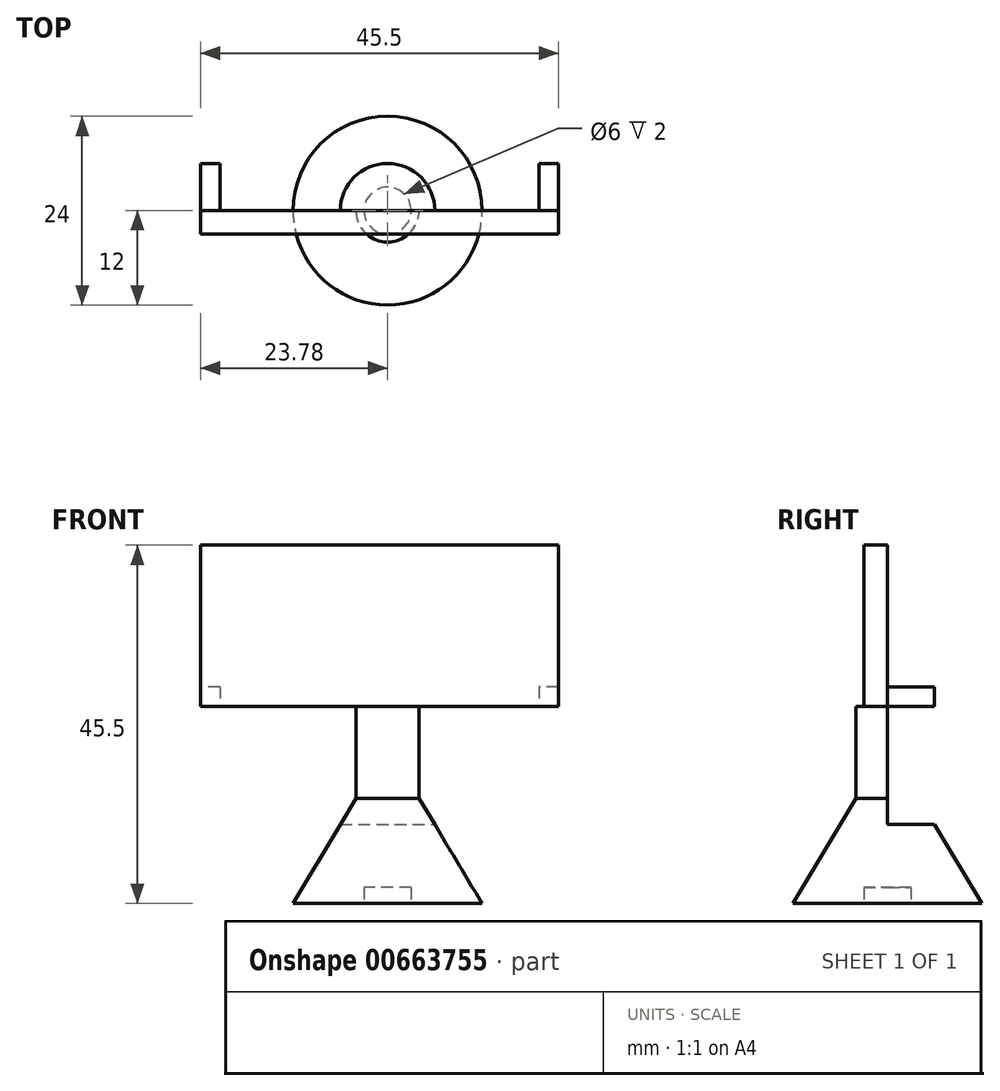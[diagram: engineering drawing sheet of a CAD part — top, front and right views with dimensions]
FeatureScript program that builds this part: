
annotation { "Feature Type Name" : "Feature", "Feature Type Description" : "" }
export const myFeature = defineFeature(function(context is Context, id is Id, definition is map)
    precondition{}
    {
        {
            var Q0;
            Q0=qCreatedBy(makeId("Front.planeOp"),FACE);
            var sketch = newSketch(context, id + "F0", { "sketchPlane" : qUnion([Q0])});
            skLineSegment(sketch, "E0", {"start": v(0, 0) * mm, "end": v(12, 0) * mm});
            skLineSegment(sketch, "E1", {"start": v(12, 0) * mm, "end": v(0, 20) * mm});
            skLineSegment(sketch, "E2", {"start": v(0, 20) * mm, "end": v(0, 0) * mm});
            skSolve(sketch);
        }
        {
            var Q0;
            Q0=makeQuery(id+"F0.imprint","IMPRINT",FACE,{"disambiguationData":[TD([[makeQuery(id+"F0.imprint","IMPRINT",EDGE,{"derivedFrom":sQuery(id+"F0.wireOp",EDGE,"E0")}),1.0]])]});
            var Q1;
            Q1=sQuery(id+"F0.wireOp",EDGE,"E2");
            revolve(context, id + "F1", {"entities" : qUnion([Q0]), "axis" : qUnion([Q1]), "revolveType" : RevolveType.FULL});
        }
        {
            var Q0;
            Q0=qCreatedBy(makeId("Top.planeOp"),FACE);
            var sketch = newSketch(context, id + "F2", { "sketchPlane" : qUnion([Q0])});
            skCircle(sketch, "E3", {"center": v(0, 0) * mm, "radius": 4 * mm});
            skSolve(sketch);
        }
        {
            var Q0;
            Q0 = qSketchRegion(id + "F2", true);
            extrude(context, id + "F3", {"entities" : qUnion([Q0]), "operationType" : NewBodyOperationType.ADD, "depth" : 25 * mm, "offsetDistance" : 25 * mm});
        }
        {
            var Q0;
            Q0=qCreatedBy(makeId("Front.planeOp"),FACE);
            var sketch = newSketch(context, id + "F4", { "sketchPlane" : qUnion([Q0])});
            skLineSegment(sketch, "E4.bottom", {"start": v(-23.78, 45.5) * mm, "end": v(21.72, 45.5) * mm});
            skLineSegment(sketch, "E4.top", {"start": v(-23.78, 25) * mm, "end": v(21.72, 25) * mm});
            skLineSegment(sketch, "E4.left", {"start": v(-23.78, 45.5) * mm, "end": v(-23.78, 25) * mm});
            skLineSegment(sketch, "E4.right", {"start": v(21.72, 45.5) * mm, "end": v(21.72, 25) * mm});
            skLineSegment(sketch, "E5.bottom", {"start": v(-23.78, 45.5) * mm, "end": v(-21.28, 45.5) * mm});
            skLineSegment(sketch, "E5.top", {"start": v(-23.78, 43) * mm, "end": v(-21.28, 43) * mm});
            skLineSegment(sketch, "E5.left", {"start": v(-23.78, 45.5) * mm, "end": v(-23.78, 43) * mm});
            skLineSegment(sketch, "E5.right", {"start": v(-21.28, 45.5) * mm, "end": v(-21.28, 43) * mm});
            skLineSegment(sketch, "E6.bottom", {"start": v(21.72, 45.5) * mm, "end": v(19.22, 45.5) * mm});
            skLineSegment(sketch, "E6.top", {"start": v(21.72, 43) * mm, "end": v(19.22, 43) * mm});
            skLineSegment(sketch, "E6.left", {"start": v(21.72, 45.5) * mm, "end": v(21.72, 43) * mm});
            skLineSegment(sketch, "E6.right", {"start": v(19.22, 45.5) * mm, "end": v(19.22, 43) * mm});
            skLineSegment(sketch, "E7.bottom", {"start": v(21.72, 27.5) * mm, "end": v(19.22, 27.5) * mm});
            skLineSegment(sketch, "E7.top", {"start": v(21.72, 25) * mm, "end": v(19.22, 25) * mm});
            skLineSegment(sketch, "E7.left", {"start": v(21.72, 27.5) * mm, "end": v(21.72, 25) * mm});
            skLineSegment(sketch, "E7.right", {"start": v(19.22, 27.5) * mm, "end": v(19.22, 25) * mm});
            skLineSegment(sketch, "E8.bottom", {"start": v(-21.28, 27.5) * mm, "end": v(-23.78, 27.5) * mm});
            skLineSegment(sketch, "E8.top", {"start": v(-21.28, 25) * mm, "end": v(-23.78, 25) * mm});
            skLineSegment(sketch, "E8.left", {"start": v(-21.28, 27.5) * mm, "end": v(-21.28, 25) * mm});
            skLineSegment(sketch, "E8.right", {"start": v(-23.78, 27.5) * mm, "end": v(-23.78, 25) * mm});
            skSolve(sketch);
        }
        {
            var Q0;
            Q0=makeQuery(id+"F4.imprint","IMPRINT",FACE,{"disambiguationData":[TD([[makeQuery(id+"F4.imprint","IMPRINT",EDGE,{"derivedFrom":sQuery(id+"F4.wireOp",EDGE,"E6.bottom")}),1.0]])]});
            var Q1;
            Q1=makeQuery(id+"F4.imprint","IMPRINT",FACE,{"disambiguationData":[TD([[makeQuery(id+"F4.imprint","IMPRINT",EDGE,{"derivedFrom":sQuery(id+"F4.wireOp",EDGE,"E8.bottom")}),1.0]])]});
            var Q2;
            Q2=makeQuery(id+"F4.imprint","IMPRINT",FACE,{"disambiguationData":[TD([[makeQuery(id+"F4.imprint","IMPRINT",EDGE,{"derivedFrom":sQuery(id+"F4.wireOp",EDGE,"E5.bottom")}),-1.0]])]});
            var Q3;
            Q3=makeQuery(id+"F4.imprint","IMPRINT",FACE,{"disambiguationData":[TD([[makeQuery(id+"F4.imprint","IMPRINT",EDGE,{"derivedFrom":sQuery(id+"F4.wireOp",EDGE,"E7.bottom")}),1.0]])]});
            extrude(context, id + "F5", {"entities" : qUnion([Q0, Q1, Q2, Q3]), "operationType" : NewBodyOperationType.ADD, "oppositeDirection" : true, "depth" : 6 * mm, "offsetDistance" : 25 * mm});
        }
        {
            var Q0;
            Q0 = qSketchRegion(id + "F4", true);
            extrude(context, id + "F6", {"entities" : qUnion([Q0]), "depth" : 3 * mm, "offsetDistance" : 25 * mm});
        }
        {
            var Q0;
            Q0=qCreatedBy(makeId("Right.planeOp"),FACE);
            var sketch = newSketch(context, id + "F7", { "sketchPlane" : qUnion([Q0])});
            skLineSegment(sketch, "E9.bottom", {"start": v(0, 25) * mm, "end": v(7.8, 25) * mm});
            skLineSegment(sketch, "E9.top", {"start": v(0, 10) * mm, "end": v(7.8, 10) * mm});
            skLineSegment(sketch, "E9.left", {"start": v(0, 25) * mm, "end": v(0, 10) * mm});
            skLineSegment(sketch, "E9.right", {"start": v(7.8, 25) * mm, "end": v(7.8, 10) * mm});
            skSolve(sketch);
        }
        {
            var Q0;
            Q0 = qSketchRegion(id + "F7", true);
            extrude(context, id + "F8", {"entities" : qUnion([Q0]), "operationType" : NewBodyOperationType.REMOVE, "endBound" : BoundingType.THROUGH_ALL, "oppositeDirection" : true, "depth" : 25 * mm, "offsetDistance" : 25 * mm});
        }
        {
            var Q0;
            Q0 = qSketchRegion(id + "F7", true);
            extrude(context, id + "F9", {"entities" : qUnion([Q0]), "operationType" : NewBodyOperationType.REMOVE, "depth" : 25 * mm, "offsetDistance" : 25 * mm});
        }
        {
            var Q0;
            Q0=qCreatedBy(makeId("Top.planeOp"),FACE);
            var sketch = newSketch(context, id + "F10", { "sketchPlane" : qUnion([Q0])});
            skCircle(sketch, "E10", {"center": v(0, 0) * mm, "radius": 3 * mm});
            skSolve(sketch);
        }
        {
            var Q0;
            Q0 = qSketchRegion(id + "F10", true);
            extrude(context, id + "F11", {"entities" : qUnion([Q0]), "operationType" : NewBodyOperationType.REMOVE, "depth" : 2 * mm, "offsetDistance" : 25 * mm});
        }
    });
